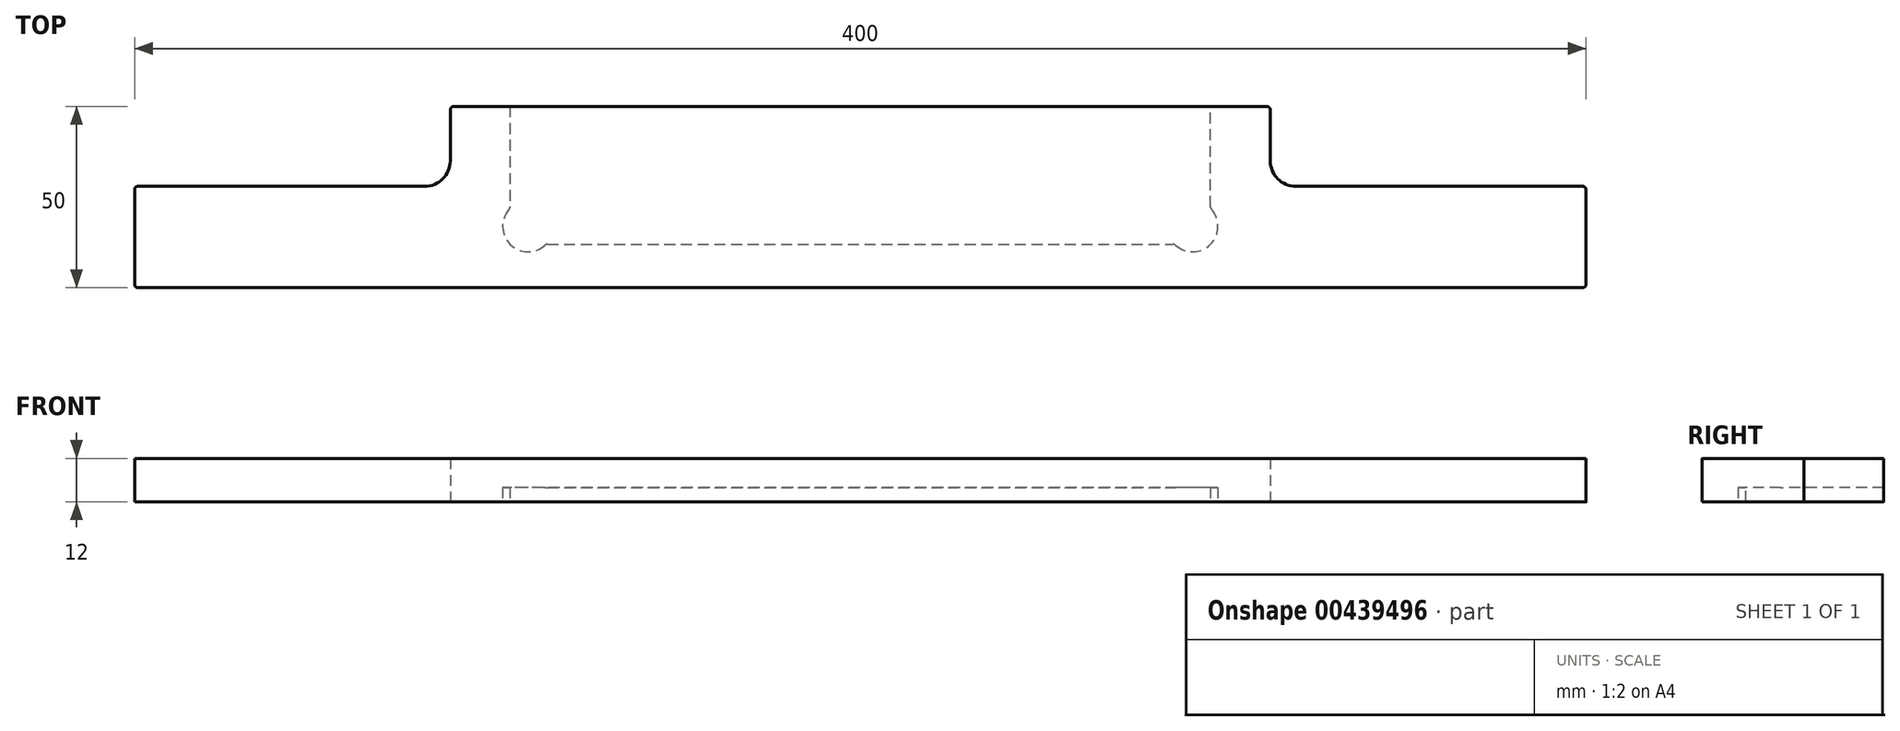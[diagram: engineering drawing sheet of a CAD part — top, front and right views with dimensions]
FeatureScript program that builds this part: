
annotation { "Feature Type Name" : "Feature", "Feature Type Description" : "" }
export const myFeature = defineFeature(function(context is Context, id is Id, definition is map)
    precondition{}
    {
        {
            var Q0;
            Q0=qCreatedBy(makeId("Top.planeOp"),FACE);
            var sketch = newSketch(context, id + "F0", { "sketchPlane" : qUnion([Q0])});
            skLineSegment(sketch, "E0", {"start": v(-200, 0) * mm, "end": v(200, 0) * mm});
            skLineSegment(sketch, "E1", {"start": v(200, 0) * mm, "end": v(200, 28) * mm});
            skLineSegment(sketch, "E2", {"start": v(200, 28) * mm, "end": v(120, 28) * mm});
            skLineSegment(sketch, "E3", {"start": v(113, 50) * mm, "end": v(-113, 50) * mm});
            skLineSegment(sketch, "E4", {"start": v(-120, 28) * mm, "end": v(-200, 28) * mm});
            skLineSegment(sketch, "E5", {"start": v(-200, 28) * mm, "end": v(-200, 0) * mm});
            skArc(sketch, "E6", {"start": v(-120, 28) * mm, "mid": v(-115.05, 30.05) * mm, "end": v(-113, 35) * mm});
            skArc(sketch, "E7", {"start": v(120, 28) * mm, "mid": v(115.05, 30.05) * mm, "end": v(113, 35) * mm});
            skLineSegment(sketch, "E8", {"start": v(113, 35) * mm, "end": v(113, 50) * mm});
            skLineSegment(sketch, "E9", {"start": v(-113, 35) * mm, "end": v(-113, 50) * mm});
            skSolve(sketch);
        }
        {
            var Q0;
            Q0=makeQuery(id+"F0.imprint","IMPRINT",FACE,{"disambiguationData":[TD([[makeQuery(id+"F0.imprint","IMPRINT",EDGE,{"derivedFrom":sQuery(id+"F0.wireOp",EDGE,"E0")}),1.0]])]});
            extrude(context, id + "F1", {"entities" : qUnion([Q0]), "depth" : 12 * mm, "offsetDistance" : 25 * mm});
        }
        {
            var Q0;
            Q0=makeQuery(id+"F1.opExtrude","CAP_FACE",FACE,{"disambiguationData":[OSD([sQuery(id+"F0.wireOp",EDGE,"E0"),sQuery(id+"F0.wireOp",EDGE,"E1"),sQuery(id+"F0.wireOp",EDGE,"E2"),sQuery(id+"F0.wireOp",EDGE,"E3"),sQuery(id+"F0.wireOp",EDGE,"E4"),sQuery(id+"F0.wireOp",EDGE,"E5"),sQuery(id+"F0.wireOp",EDGE,"E6"),sQuery(id+"F0.wireOp",EDGE,"E7")])],"isStart":true});
            var sketch = newSketch(context, id + "F2", { "sketchPlane" : qUnion([Q0])});
            skLineSegment(sketch, "E10", {"start": v(-96.5, -50) * mm, "end": v(96.5, -50) * mm});
            skPoint(sketch, "E11", {"position": v(0, -50) * mm});
            skLineSegment(sketch, "E12", {"start": v(-96.5, -50) * mm, "end": v(-96.5, -21.9) * mm});
            skArc(sketch, "E13", {"start": v(-96.5, -21.9) * mm, "mid": v(-96.5, -12) * mm, "end": v(-86.6, -12) * mm});
            skLineSegment(sketch, "E14", {"start": v(-86.6, -12) * mm, "end": v(86.6, -12) * mm});
            skArc(sketch, "E15", {"start": v(86.6, -12) * mm, "mid": v(96.5, -12) * mm, "end": v(96.5, -21.9) * mm});
            skLineSegment(sketch, "E16", {"start": v(96.5, -21.9) * mm, "end": v(96.5, -50) * mm});
            skLineSegment(sketch, "E17", {"start": v(-86.6, -12) * mm, "end": v(-96.5, -12) * mm, "construction": true});
            skLineSegment(sketch, "E18", {"start": v(-96.5, -12) * mm, "end": v(-96.5, -21.9) * mm, "construction": true});
            skLineSegment(sketch, "E19", {"start": v(86.6, -12) * mm, "end": v(96.5, -12) * mm, "construction": true});
            skLineSegment(sketch, "E20", {"start": v(96.5, -12) * mm, "end": v(96.5, -21.9) * mm, "construction": true});
            skSolve(sketch);
        }
        {
            var Q0;
            Q0 = qSketchRegion(id + "F2", true);
            extrude(context, id + "F3", {"entities" : qUnion([Q0]), "operationType" : NewBodyOperationType.REMOVE, "oppositeDirection" : true, "depth" : 4 * mm, "offsetDistance" : 25 * mm});
        }
        {
            var Q0;
            Q0=makeQuery(id+"F1.opExtrude","SWEPT_EDGE",EDGE,{"disambiguationData":[OSD([sQuery(id+"F0.wireOp",EDGE,"E0"),sQuery(id+"F0.wireOp",EDGE,"E5")])]});
            var Q1;
            Q1=makeQuery(id+"F1.opExtrude","SWEPT_EDGE",EDGE,{"disambiguationData":[OSD([sQuery(id+"F0.wireOp",EDGE,"E4"),sQuery(id+"F0.wireOp",EDGE,"E5")])]});
            var Q2;
            Q2=makeQuery(id+"F1.opExtrude","SWEPT_EDGE",EDGE,{"disambiguationData":[OSD([sQuery(id+"F0.wireOp",EDGE,"E3"),sQuery(id+"F0.wireOp",EDGE,"E9")])]});
            var Q3;
            Q3=makeQuery(id+"F3.boolean.opBoolean","COPY",EDGE,{"derivedFrom":makeQuery(id+"F3.opExtrude","SWEPT_EDGE",EDGE,{"disambiguationData":[OSD([sQuery(id+"F2.wireOp",EDGE,"E12"),sQuery(id+"F2.wireOp",EDGE,"E13")])]})});
            var Q4;
            Q4=makeQuery(id+"F3.boolean.opBoolean","COPY",EDGE,{"derivedFrom":makeQuery(id+"F3.opExtrude","SWEPT_EDGE",EDGE,{"disambiguationData":[OSD([sQuery(id+"F2.wireOp",EDGE,"E13"),sQuery(id+"F2.wireOp",EDGE,"E14")])]})});
            var Q5;
            Q5=makeQuery(id+"F3.boolean.opBoolean","COPY",EDGE,{"derivedFrom":makeQuery(id+"F3.opExtrude","SWEPT_EDGE",EDGE,{"disambiguationData":[OSD([sQuery(id+"F2.wireOp",EDGE,"E14"),sQuery(id+"F2.wireOp",EDGE,"E15")])]})});
            var Q6;
            Q6=makeQuery(id+"F3.boolean.opBoolean","COPY",EDGE,{"derivedFrom":makeQuery(id+"F3.opExtrude","SWEPT_EDGE",EDGE,{"disambiguationData":[OSD([sQuery(id+"F2.wireOp",EDGE,"E15"),sQuery(id+"F2.wireOp",EDGE,"E16")])]})});
            var Q7;
            Q7=makeQuery(id+"F1.opExtrude","SWEPT_EDGE",EDGE,{"disambiguationData":[OSD([sQuery(id+"F0.wireOp",EDGE,"E3"),sQuery(id+"F0.wireOp",EDGE,"E8")])]});
            var Q8;
            Q8=makeQuery(id+"F1.opExtrude","SWEPT_EDGE",EDGE,{"disambiguationData":[OSD([sQuery(id+"F0.wireOp",EDGE,"E1"),sQuery(id+"F0.wireOp",EDGE,"E2")])]});
            var Q9;
            Q9=makeQuery(id+"F1.opExtrude","SWEPT_EDGE",EDGE,{"disambiguationData":[OSD([sQuery(id+"F0.wireOp",EDGE,"E0"),sQuery(id+"F0.wireOp",EDGE,"E1")])]});
            fillet(context, id + "F4", {"entities" : qUnion([Q0, Q1, Q2, Q3, Q4, Q5, Q6, Q7, Q8, Q9]), "radius" : 1 * mm, "tangentPropagation" : true, "allowEdgeOverflow" : false});
        }
    });
